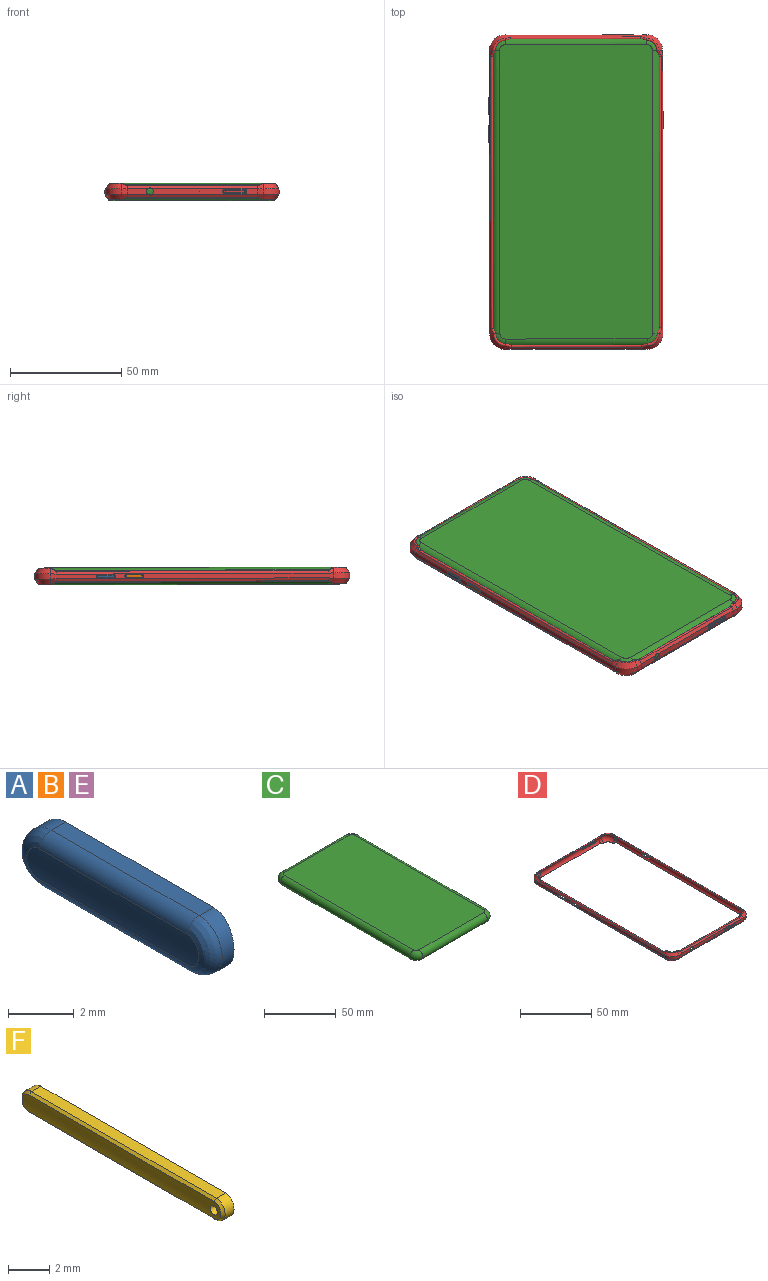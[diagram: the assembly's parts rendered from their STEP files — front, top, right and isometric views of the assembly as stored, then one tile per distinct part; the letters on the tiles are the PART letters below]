
ASSEMBLY  parts=6 mates=8
PART A: 10 faces, bbox 1.2x8.4x2 mm
  f0: plane 6.35x0.62mm, normal (0,0,1), area 3.9mm2, adj f3,f4,f5,f6
  f1: cylinder r=4.83mm len=7.37mm, axis (0,1,0), area 8.1mm2, adj f6,f7,f8,f9
  f2: plane 6.35x0.62mm, normal (0,0,-1), area 3.9mm2, adj f3,f4,f5,f9
  f3: cylinder r=3.81mm len=8.38mm, axis (0,1,0), area 16.3mm2, adj f0,f2,f4,f5
  f4: cylinder r=1.02mm len=2.03mm, axis (1,0,0), area 1.8mm2, adj f0,f2,f3,f8
  f5: cylinder r=1.02mm len=2.03mm, axis (1,0,0), area 1.8mm2, adj f0,f2,f3,f7
  f6: cylinder r=0.51mm len=6.35mm, axis (0,1,0), area 4.7mm2, adj f0,f1,f7,f8
  f7: bspline ~2.03x1.24mm, area 2mm2, adj f1,f5,f6,f9
  f8: bspline ~2.03x1.24mm, area 2mm2, adj f1,f4,f6,f9
  f9: cylinder r=0.51mm len=6.35mm, axis (0,1,0), area 4.7mm2, adj f1,f2,f7,f8
PART B: same geometry as A
PART C: 10 faces, bbox 76.2x139.7x7.6 mm
  f0: plane 132.08x68.58mm, normal (0,0,1), area 9052.5mm2, adj f2,f3,f4,f5,f6,f7,f8,f9
  f1: plane 132.08x68.58mm, normal (0,0,-1), area 9052.5mm2, adj f2,f3,f4,f5,f6,f7,f8,f9
  f2: cylinder r=3.81mm len=127mm, axis (0,1,0), area 1520.1mm2, adj f0,f1,f3,f4
  f3: torus R=2.54mm, axis (0,0,1), area 93.4mm2, adj f0,f1,f2,f5
  f4: torus R=2.54mm, axis (0,0,1), area 93.4mm2, adj f0,f1,f2,f6
  f5: cylinder r=3.81mm len=63.5mm, axis (-1,0,0), area 760.1mm2, adj f0,f1,f3,f7
  f6: cylinder r=3.81mm len=63.5mm, axis (1,0,0), area 760.1mm2, adj f0,f1,f4,f8
  f7: torus R=2.54mm, axis (0,0,1), area 93.4mm2, adj f0,f1,f5,f9
  f8: torus R=2.54mm, axis (0,0,1), area 93.4mm2, adj f0,f1,f6,f9
  f9: cylinder r=3.81mm len=127mm, axis (0,-1,0), area 1520.1mm2, adj f0,f1,f7,f8
PART D: 146 faces, bbox 78.1x141.6x7.8 mm
  f0: plane 6.02x2.54mm, normal (0,-1,0), area 12.8mm2, adj f8,f14,f51,f128
  f1: plane 33.01x2.54mm, normal (0,-1,0), area 80.1mm2, adj f8,f14,f125,f126,f134
  f2: plane 9.21x2.54mm, normal (0,-1,0), area 22.3mm2, adj f8,f14,f25,f125
  f3: plane 6.35x2.03mm, normal (-1,0,0), area 9.7mm2, adj f30,f35,f120,f122
  f4: plane 86.36x2.54mm, normal (-1,0,0), area 174.5mm2, adj f15,f30,f35,f37,f38,f118
  f5: cylinder r=3.81mm len=121.92mm, axis (0,1,0), area 615.9mm2, adj f32,f33,f40,f93,f117,f118,f119,f120
  f6: plane 92.71x2.54mm, normal (1,0,0), area 187.4mm2, adj f41,f56,f61,f63,f64,f114
  f7: cylinder r=3.81mm len=121.92mm, axis (0,1,0), area 632.3mm2, adj f58,f59,f66,f112,f113,f114,f115,f116
  f8: plane 58.52x1.49mm, normal (0,-0.85,-0.52), area 95.5mm2, adj f0,f1,f2,f9,f26,f52,f125,f127
  f9: cylinder r=0.64mm len=58.42mm, axis (1,0,0), area 64.3mm2, adj f8,f10,f27,f53
  f10: plane 58.42x0.05mm, normal (0,0.71,-0.71), area 4.4mm2, adj f9,f11,f27,f53
  f11: cylinder r=3.81mm len=58.42mm, axis (1,0,0), area 341.5mm2, adj f10,f12,f28,f54,f125,f126
  f12: plane 58.42x0.05mm, normal (0,0.71,0.71), area 4.4mm2, adj f11,f13,f23,f49
  f13: cylinder r=0.64mm len=58.42mm, axis (1,0,0), area 64.3mm2, adj f12,f14,f23,f49
  f14: plane 58.81x1.79mm, normal (0,-0.85,0.52), area 95.5mm2, adj f0,f1,f2,f13,f24,f50,f125,f129
  f15: cylinder r=7.11mm len=7.11mm, axis (0,0,1), area 28.4mm2, adj f4,f16,f22,f25
  f16: cone r=7.11mm half-angle=36.5deg, axis (0,0,1), area 27.8mm2, adj f15,f17,f26,f38
  f17: torus R=5.03mm, axis (0,0,1), area 8.5mm2, adj f16,f18,f27,f39
  f18: cone r=4.48mm half-angle=30deg, axis (0,0,-1), area 0.5mm2, adj f17,f19,f27,f39
  f19: torus R=2.54mm, axis (0,0,1), area 71.3mm2, adj f18,f20,f28,f40
  f20: cone r=4.45mm half-angle=30deg, axis (0,0,1), area 0.5mm2, adj f19,f21,f23,f36
  f21: torus R=5.03mm, axis (0,0,1), area 8.5mm2, adj f20,f22,f23,f36
  f22: cone r=5.43mm half-angle=36.5deg, axis (0,0,-1), area 27.8mm2, adj f15,f21,f24,f37
  f23: bspline ~2.54x1.64mm, area 3.1mm2, adj f12,f13,f20,f21,f24,f28
  f24: bspline ~2.54x2.27mm, area 5.7mm2, adj f14,f22,f23,f25
  f25: bspline ~2.54x2.54mm, area 6.5mm2, adj f2,f15,f24,f26
  f26: bspline ~2.54x2.27mm, area 5.7mm2, adj f8,f16,f25,f27
  f27: bspline ~2.54x1.64mm, area 3.1mm2, adj f9,f10,f17,f18,f26,f28
  f28: bspline ~6.6x2.54mm, area 17.7mm2, adj f11,f19,f23,f27
  f29: plane 21.59x2.54mm, normal (-1,0,0), area 42.9mm2, adj f30,f35,f75,f90,f91,f124
  f30: plane 121.92x1.32mm, normal (-0.9,0,-0.44), area 178.9mm2, adj f3,f4,f29,f31,f38,f91,f117,f121
  f31: cylinder r=0.64mm len=121.92mm, axis (0,1,0), area 134.2mm2, adj f30,f32,f39,f92
  f32: plane 121.92x0.06mm, normal (0.64,0,-0.77), area 9.2mm2, adj f5,f31,f39,f92
  f33: plane 121.92x0.06mm, normal (0.64,0,0.77), area 9.2mm2, adj f5,f34,f36,f89
  f34: cylinder r=0.64mm len=121.92mm, axis (0,1,0), area 134.2mm2, adj f33,f35,f36,f89
  f35: plane 121.92x1.32mm, normal (-0.9,0,0.44), area 178.9mm2, adj f3,f4,f29,f34,f37,f90,f119,f123
  f36: bspline ~2.54x2.03mm, area 3.2mm2, adj f20,f21,f33,f34,f37,f40
  f37: bspline ~2.54x2.52mm, area 5.4mm2, adj f4,f22,f35,f36
  f38: bspline ~2.54x2.52mm, area 5.4mm2, adj f4,f16,f30,f39
  f39: bspline ~2.54x2.03mm, area 3.2mm2, adj f17,f18,f31,f32,f38,f40
  f40: bspline ~6.6x2.54mm, area 16.9mm2, adj f5,f19,f36,f39
  f41: cylinder r=7.11mm len=7.11mm, axis (0,0,1), area 28.4mm2, adj f6,f42,f48,f51
  f42: cone r=7.11mm half-angle=36.5deg, axis (0,0,1), area 27.8mm2, adj f41,f43,f52,f64
  f43: torus R=5.03mm, axis (0,0,1), area 8.5mm2, adj f42,f44,f53,f65
  f44: cone r=4.48mm half-angle=30deg, axis (0,0,-1), area 0.5mm2, adj f43,f45,f53,f65
  f45: torus R=2.54mm, axis (0,0,1), area 71.3mm2, adj f44,f46,f54,f66
  f46: cone r=4.45mm half-angle=30deg, axis (0,0,1), area 0.5mm2, adj f45,f47,f49,f62
  f47: torus R=5.03mm, axis (0,0,1), area 8.5mm2, adj f46,f48,f49,f62
  f48: cone r=5.43mm half-angle=36.5deg, axis (0,0,-1), area 27.8mm2, adj f41,f47,f50,f63
  f49: bspline ~2.54x1.64mm, area 3.1mm2, adj f12,f13,f46,f47,f50,f54
  f50: bspline ~2.54x2.27mm, area 5.7mm2, adj f14,f48,f49,f51
  f51: bspline ~2.54x2.54mm, area 6.5mm2, adj f0,f41,f50,f52
  f52: bspline ~2.54x2.27mm, area 5.7mm2, adj f8,f42,f51,f53
  f53: bspline ~2.54x1.64mm, area 3.1mm2, adj f9,f10,f43,f44,f52,f54
  f54: bspline ~6.6x2.54mm, area 17.7mm2, adj f11,f45,f49,f53
  f55: plane 27.94x2.54mm, normal (1,0,0), area 55.8mm2, adj f56,f61,f94,f109,f110,f116
  f56: plane 121.92x1.32mm, normal (0.9,0,-0.44), area 178.9mm2, adj f6,f55,f57,f64,f110,f115
  f57: cylinder r=0.64mm len=121.92mm, axis (0,1,0), area 134.2mm2, adj f56,f58,f65,f111
  f58: plane 121.92x0.06mm, normal (-0.64,0,-0.77), area 9.2mm2, adj f7,f57,f65,f111
  f59: plane 121.92x0.06mm, normal (-0.64,0,0.77), area 9.2mm2, adj f7,f60,f62,f108
  f60: cylinder r=0.64mm len=121.92mm, axis (0,1,0), area 134.2mm2, adj f59,f61,f62,f108
  f61: plane 121.92x1.32mm, normal (0.9,0,0.44), area 178.9mm2, adj f6,f55,f60,f63,f109,f113
  f62: bspline ~2.54x2.03mm, area 3.2mm2, adj f46,f47,f59,f60,f63,f66
  f63: bspline ~2.54x2.52mm, area 5.4mm2, adj f6,f48,f61,f62
  f64: bspline ~2.54x2.52mm, area 5.4mm2, adj f6,f42,f56,f65
  f65: bspline ~2.54x2.03mm, area 3.2mm2, adj f43,f44,f57,f58,f64,f66
  f66: bspline ~6.6x2.54mm, area 16.9mm2, adj f7,f45,f62,f65
  f67: plane 58.42x2.54mm, normal (0,1,0), area 131mm2, adj f68,f74,f85,f104,f142,f143,f144,f145
  f68: plane 58.42x1.4mm, normal (0,0.85,-0.52), area 95.9mm2, adj f67,f69,f86,f105
  f69: cylinder r=0.64mm len=58.42mm, axis (1,0,0), area 64.3mm2, adj f68,f70,f87,f106
  f70: plane 58.42x0.05mm, normal (0,-0.71,-0.71), area 4.4mm2, adj f69,f71,f87,f106
  f71: cylinder r=3.81mm len=58.42mm, axis (1,0,0), area 333.4mm2, adj f70,f72,f88,f107,f142,f143,f144,f145
  f72: plane 58.42x0.05mm, normal (0,-0.71,0.71), area 4.4mm2, adj f71,f73,f83,f102
  f73: cylinder r=0.64mm len=58.42mm, axis (1,0,0), area 64.3mm2, adj f72,f74,f83,f102
  f74: plane 58.42x1.4mm, normal (0,0.85,0.52), area 95.9mm2, adj f67,f73,f84,f103
  f75: cylinder r=7.11mm len=7.11mm, axis (0,0,1), area 28.4mm2, adj f29,f76,f82,f85
  f76: cone r=7.11mm half-angle=36.5deg, axis (0,0,1), area 27.8mm2, adj f75,f77,f86,f91
  f77: torus R=5.03mm, axis (0,0,1), area 8.5mm2, adj f76,f78,f87,f92
  f78: cone r=4.48mm half-angle=30deg, axis (0,0,-1), area 0.5mm2, adj f77,f79,f87,f92
  f79: torus R=2.54mm, axis (0,0,1), area 71.3mm2, adj f78,f80,f88,f93
  f80: cone r=4.45mm half-angle=30deg, axis (0,0,1), area 0.5mm2, adj f79,f81,f83,f89
  f81: torus R=5.03mm, axis (0,0,1), area 8.5mm2, adj f80,f82,f83,f89
  f82: cone r=5.43mm half-angle=36.5deg, axis (0,0,-1), area 27.8mm2, adj f75,f81,f84,f90
  f83: bspline ~2.54x1.64mm, area 3.1mm2, adj f72,f73,f80,f81,f84,f88
  f84: bspline ~2.54x2.27mm, area 5.7mm2, adj f74,f82,f83,f85
  f85: bspline ~2.54x2.54mm, area 6.5mm2, adj f67,f75,f84,f86
  f86: bspline ~2.54x2.27mm, area 5.7mm2, adj f68,f76,f85,f87
  f87: bspline ~2.54x1.64mm, area 3.1mm2, adj f69,f70,f77,f78,f86,f88
  f88: bspline ~6.6x2.54mm, area 17.7mm2, adj f71,f79,f83,f87
  f89: bspline ~2.54x2.03mm, area 3.2mm2, adj f33,f34,f80,f81,f90,f93
  f90: bspline ~2.54x2.52mm, area 5.4mm2, adj f29,f35,f82,f89
  f91: bspline ~2.54x2.52mm, area 5.4mm2, adj f29,f30,f76,f92
  f92: bspline ~2.54x2.03mm, area 3.2mm2, adj f31,f32,f77,f78,f91,f93
  f93: bspline ~6.6x2.54mm, area 16.9mm2, adj f5,f79,f89,f92
  f94: cylinder r=7.11mm len=7.11mm, axis (0,0,1), area 28.4mm2, adj f55,f95,f101,f104
  f95: cone r=7.11mm half-angle=36.5deg, axis (0,0,1), area 27.8mm2, adj f94,f96,f105,f110
  f96: torus R=5.03mm, axis (0,0,1), area 8.5mm2, adj f95,f97,f106,f111
  f97: cone r=4.48mm half-angle=30deg, axis (0,0,-1), area 0.5mm2, adj f96,f98,f106,f111
  f98: torus R=2.54mm, axis (0,0,1), area 71.3mm2, adj f97,f99,f107,f112
  f99: cone r=4.45mm half-angle=30deg, axis (0,0,1), area 0.5mm2, adj f98,f100,f102,f108
  f100: torus R=5.03mm, axis (0,0,1), area 8.5mm2, adj f99,f101,f102,f108
  f101: cone r=5.43mm half-angle=36.5deg, axis (0,0,-1), area 27.8mm2, adj f94,f100,f103,f109
  f102: bspline ~2.54x1.64mm, area 3.1mm2, adj f72,f73,f99,f100,f103,f107
  f103: bspline ~2.54x2.27mm, area 5.7mm2, adj f74,f101,f102,f104
  f104: bspline ~2.54x2.54mm, area 6.5mm2, adj f67,f94,f103,f105
  f105: bspline ~2.54x2.27mm, area 5.7mm2, adj f68,f95,f104,f106
  f106: bspline ~2.54x1.64mm, area 3.1mm2, adj f69,f70,f96,f97,f105,f107
  f107: bspline ~6.6x2.54mm, area 17.7mm2, adj f71,f98,f102,f106
  f108: bspline ~2.54x2.03mm, area 3.2mm2, adj f59,f60,f99,f100,f109,f112
  f109: bspline ~2.54x2.52mm, area 5.4mm2, adj f55,f61,f101,f108
  f110: bspline ~2.54x2.52mm, area 5.4mm2, adj f55,f56,f95,f111
  f111: bspline ~2.54x2.03mm, area 3.2mm2, adj f57,f58,f96,f97,f110,f112
  f112: bspline ~6.6x2.54mm, area 16.9mm2, adj f7,f98,f108,f111
  f113: plane 6.35x0.9mm, normal (0,0,-1), area 5.7mm2, adj f7,f61,f114,f116
  f114: cylinder r=1.02mm len=2.03mm, axis (1,0,0), area 2.9mm2, adj f6,f7,f113,f115
  f115: plane 6.35x0.9mm, normal (0,0,1), area 5.7mm2, adj f7,f56,f114,f116
  f116: cylinder r=1.02mm len=2.03mm, axis (1,0,0), area 2.9mm2, adj f7,f55,f113,f115
  f117: plane 6.35x0.9mm, normal (0,0,1), area 5.7mm2, adj f5,f30,f118,f120
  f118: cylinder r=1.02mm len=2.03mm, axis (-1,0,0), area 2.9mm2, adj f4,f5,f117,f119
  f119: plane 6.35x0.9mm, normal (0,0,-1), area 5.7mm2, adj f5,f35,f118,f120
  f120: cylinder r=1.02mm len=2.03mm, axis (-1,0,0), area 2.9mm2, adj f3,f5,f117,f119
  f121: plane 6.35x0.9mm, normal (0,0,1), area 5.7mm2, adj f5,f30,f122,f124
  f122: cylinder r=1.02mm len=2.03mm, axis (-1,0,0), area 2.9mm2, adj f3,f5,f121,f123
  f123: plane 6.35x0.9mm, normal (0,0,-1), area 5.7mm2, adj f5,f35,f122,f124
  f124: cylinder r=1.02mm len=2.03mm, axis (-1,0,0), area 2.9mm2, adj f5,f29,f121,f123
  f125: cylinder r=1.59mm len=3.18mm, axis (0,-1,0), area 10.9mm2, adj f1,f2,f8,f11,f14
  f126: cylinder r=0.13mm len=0.76mm, axis (0,-1,0), area 0.6mm2, adj f1,f11
  f127: plane 8.28x0.38mm, normal (0,0,1), area 3.2mm2, adj f8,f128,f134,f135
  f128: cylinder r=1.27mm len=2.54mm, axis (0,-1,0), area 1.5mm2, adj f0,f127,f129,f135
  f129: plane 8.28x0.38mm, normal (0,0,-1), area 3.2mm2, adj f14,f128,f134,f135
  f130: plane 8.28x0.38mm, normal (0,0,-1), area 3.2mm2, adj f131,f133,f135,f136
  f131: cylinder r=0.89mm len=1.78mm, axis (0,-1,0), area 1.1mm2, adj f130,f132,f135,f136
  f132: plane 8.28x0.38mm, normal (0,0,1), area 3.2mm2, adj f131,f133,f135,f136
  f133: cylinder r=0.89mm len=1.78mm, axis (0,-1,0), area 1.1mm2, adj f130,f132,f135,f136
  f134: cylinder r=1.27mm len=2.54mm, axis (0,-1,0), area 1.5mm2, adj f1,f127,f129,f135
  f135: plane 10.82x2.54mm, normal (0,-1,0), area 8.9mm2, adj f127,f128,f129,f130,f131,f132,f133,f134
  f136: plane 10.06x1.78mm, normal (0,-1,0), area 12.8mm2, adj f130,f131,f132,f133,f137,f138,f139,f140
  f137: cylinder r=0.25mm len=0.51mm, axis (0,-1,0), area 0.3mm2, adj f136,f138,f140,f141
  f138: plane 8.28x0.38mm, normal (0,0,1), area 3.2mm2, adj f136,f137,f139,f141
  f139: cylinder r=0.25mm len=0.51mm, axis (0,-1,0), area 0.3mm2, adj f136,f138,f140,f141
  f140: plane 8.28x0.38mm, normal (0,0,-1), area 3.2mm2, adj f136,f137,f139,f141
  f141: plane 8.79x0.51mm, normal (0,-1,0), area 4.4mm2, adj f137,f138,f139,f140
  f142: plane 12.7x0.82mm, normal (0,0,1), area 10.4mm2, adj f67,f71,f143,f145
  f143: cylinder r=0.64mm len=1.27mm, axis (0,1,0), area 1.6mm2, adj f67,f71,f142,f144
  f144: plane 12.7x0.82mm, normal (0,0,-1), area 10.4mm2, adj f67,f71,f143,f145
  f145: cylinder r=0.64mm len=1.27mm, axis (0,1,0), area 1.6mm2, adj f67,f71,f142,f144
PART E: same geometry as A
PART F: 11 faces, bbox 0.8x14x1.3 mm
  f0: cylinder r=3.81mm len=13.97mm, axis (0,1,0), area 17.3mm2, adj f1,f2,f3,f4,f5
  f1: cylinder r=0.64mm len=1.27mm, axis (1,0,0), area 1.3mm2, adj f0,f2,f4,f8
  f2: plane 12.7x0.64mm, normal (0,0,-1), area 8.2mm2, adj f0,f1,f3,f7
  f3: cylinder r=0.64mm len=1.27mm, axis (1,0,0), area 1.3mm2, adj f0,f2,f4,f9
  f4: plane 12.7x0.64mm, normal (0,0,1), area 8.2mm2, adj f0,f1,f3,f10
  f5: cylinder r=0.25mm len=0.76mm, axis (1,0,0), area 1.2mm2, adj f0,f6
  f6: cylinder r=4.57mm len=13.68mm, axis (0,1,0), area 13.4mm2, adj f5,f7,f8,f9,f10
  f7: plane 12.7x0.15mm, normal (-0.67,0,-0.75), area 2.5mm2, adj f2,f6,f8,f9
  f8: bspline ~1.29x0.64mm, area 0.4mm2, adj f1,f6,f7,f10
  f9: bspline ~1.29x0.64mm, area 0.4mm2, adj f3,f6,f7,f10
  f10: plane 12.7x0.15mm, normal (-0.67,0,0.75), area 2.5mm2, adj f4,f6,f8,f9
PLACE A rot(axis=(-0.9,-0.01,0.44),0.2deg) t=(42.2,50.1,-37.14)mm
PLACE B rot(axis=(1,0,0),179.8deg) t=(42.24,24.7,-37.05)mm
PLACE C rot(axis=(-0.9,-0.01,0.44),0.2deg) t=(38.58,-64.68,-40.57)mm
PLACE D rot(axis=(-0.9,-0.01,0.44),0.2deg) t=(38.46,5.01,-36.99)mm
PLACE E rot(axis=(0,0,-1),179.9deg) t=(110.81,31.16,-37.07)mm
PLACE F rot(axis=(0,0,-1),89.9deg) t=(105.03,71.33,-37.2)mm
MATE cylindrical C.f2 <-> D.f5  axis (0,1,0) through (42.27,5.19,-36.99)mm
MATE cylindrical F.f1 <-> D.f145  axis (0,-1,0) through (101.85,75.41,-37.22)mm
MATE cylindrical C.f6 <-> F.f0  axis (1,0,0) through (76.46,71.28,-37.2)mm
MATE cylindrical E.f1 <-> C.f9  axis (0,-1,0) through (110.8,37.51,-37.09)mm
MATE cylindrical D.f11 <-> C.f5  axis (1,0,0) through (76.67,-60.8,-36.77)mm
MATE cylindrical D.f124 <-> A.f4  axis (-1,0,0) through (38.09,46.92,-37.13)mm
MATE cylindrical B.f5 <-> D.f114  axis (1,0,0) through (38.23,34.22,-37.08)mm
MATE cylindrical E.f4 <-> D.f114  axis (-1,0,0) through (114.8,34.35,-37.08)mm
